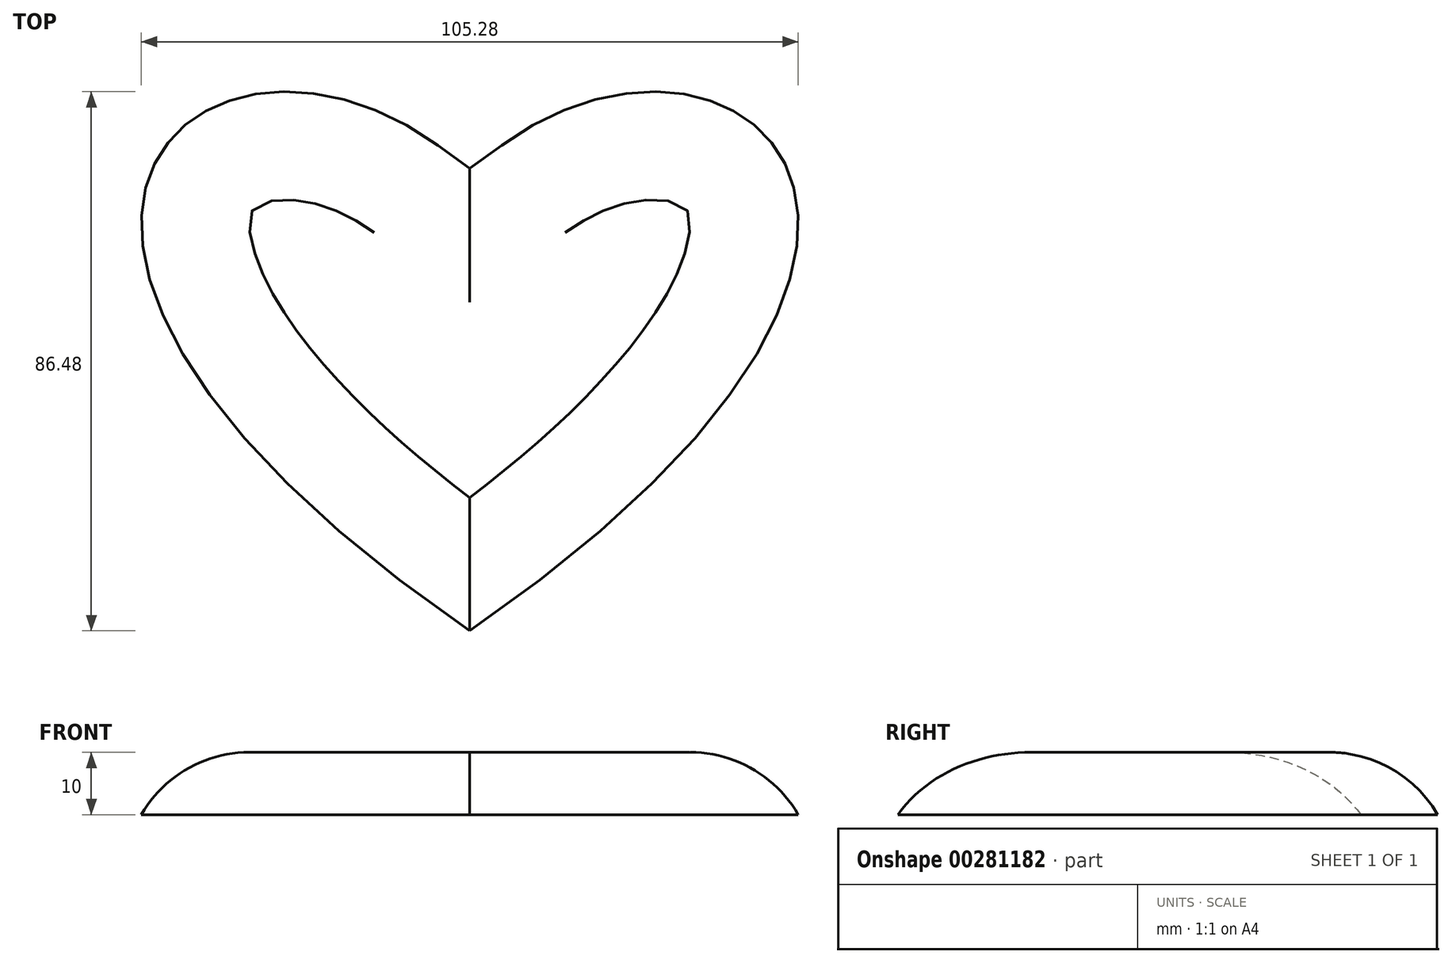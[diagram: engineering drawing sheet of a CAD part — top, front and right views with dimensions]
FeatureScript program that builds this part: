
annotation { "Feature Type Name" : "Feature", "Feature Type Description" : "" }
export const myFeature = defineFeature(function(context is Context, id is Id, definition is map)
    precondition{}
    {
        {
            var Q0;
            Q0=qCreatedBy(makeId("Top.planeOp"),FACE);
            var sketch = newSketch(context, id + "F0", { "sketchPlane" : qUnion([Q0])});
            skFitSpline(sketch, "E0", {"points": [v(0, 0) * mm, v(-5.1, 77.87) * mm], "startDerivative": vector(-276.75, 190.26) * mm, "endDerivative": vector(113.34, -82.65) * mm});
            skLineSegment(sketch, "E1", {"start": v(-5.1, 77.87) * mm, "end": v(0, 74.15) * mm});
            skLineSegment(sketch, "E2", {"start": v(0, 0) * mm, "end": v(0, 74.15) * mm, "construction": true});
            skFitSpline(sketch, "E3.MirrorCS", {"points": [v(0, 0) * mm, v(5.1, 77.87) * mm], "startDerivative": vector(276.75, 190.26) * mm, "endDerivative": vector(-113.34, -82.65) * mm});
            skLineSegment(sketch, "E4.MirrorCS", {"start": v(5.1, 77.87) * mm, "end": v(0, 74.15) * mm});
            skSolve(sketch);
        }
        {
            var Q0;
            Q0=makeQuery(id+"F0.imprint","IMPRINT",FACE,{"disambiguationData":[TD([[makeQuery(id+"F0.imprint","IMPRINT",EDGE,{"derivedFrom":sQuery(id+"F0.wireOp",EDGE,"E0")}),-1.0]])]});
            extrude(context, id + "F1", {"entities" : qUnion([Q0]), "depth" : 10 * mm});
        }
        {
            var Q0;
            Q0=makeQuery(id+"F1.opExtrude","CAP_EDGE",EDGE,{"disambiguationData":[OSD([sQuery(id+"F0.wireOp",EDGE,"E0")])],"isStart":false});
            var Q1;
            Q1=makeQuery(id+"F1.opExtrude","CAP_EDGE",EDGE,{"disambiguationData":[OSD([sQuery(id+"F0.wireOp",EDGE,"E3.MirrorCS")])],"isStart":false});
            fillet(context, id + "F2", {"entities" : qUnion([Q0, Q1]), "radius" : 20 * mm, "tangentPropagation" : true, "allowEdgeOverflow" : false});
        }
    });
